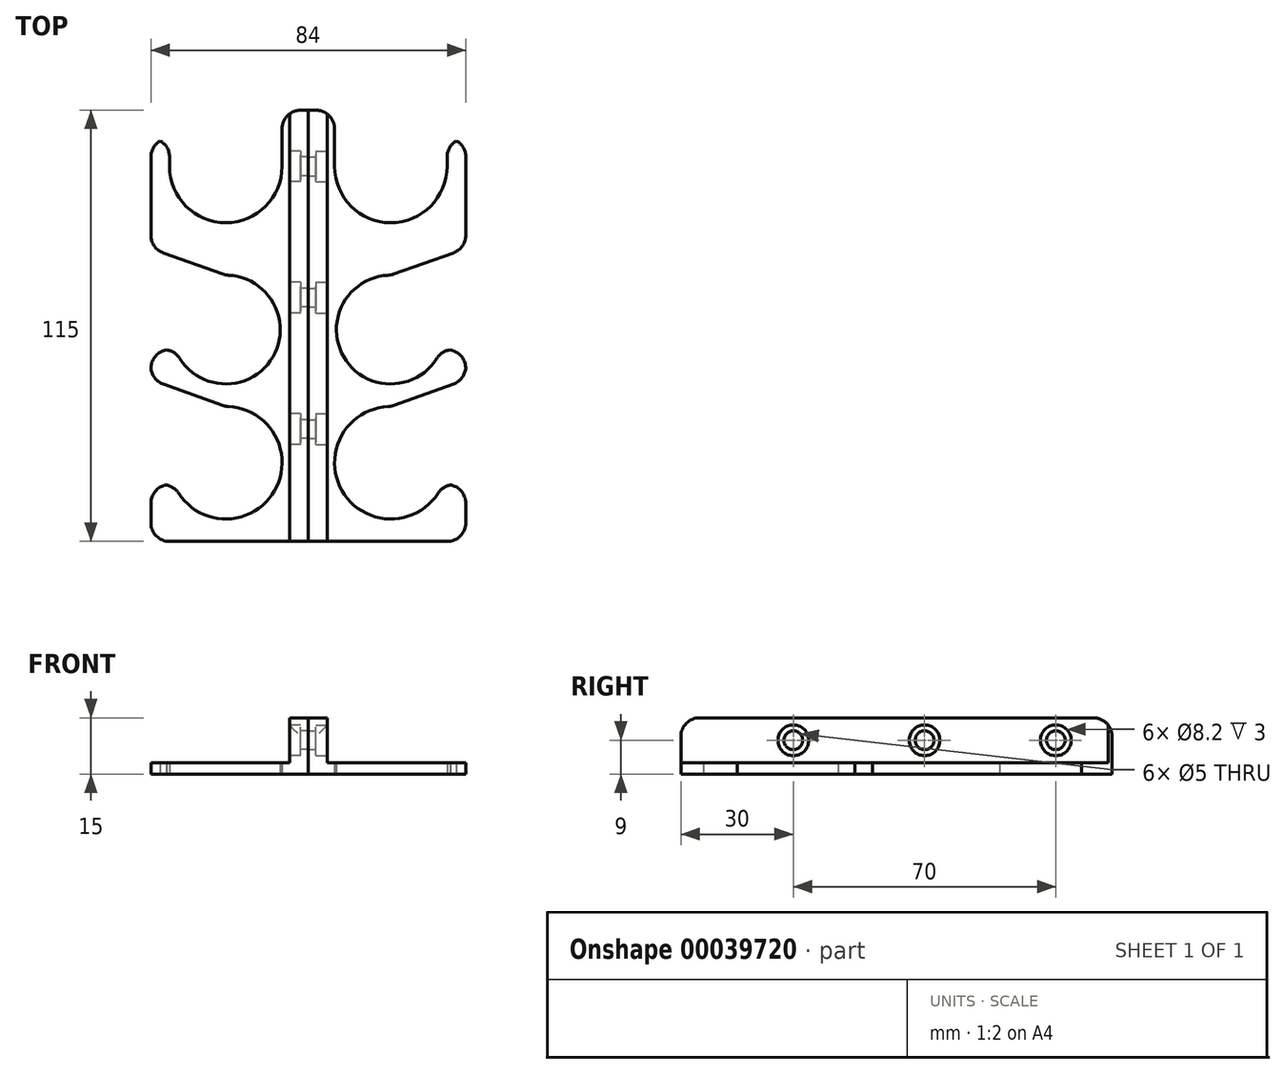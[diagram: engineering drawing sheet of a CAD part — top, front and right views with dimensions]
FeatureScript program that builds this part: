
annotation { "Feature Type Name" : "Feature", "Feature Type Description" : "" }
export const myFeature = defineFeature(function(context is Context, id is Id, definition is map)
    precondition{}
    {
        {
            var Q0;
            Q0=qCreatedBy(makeId("Top.planeOp"),FACE);
            var sketch = newSketch(context, id + "F0", { "sketchPlane" : qUnion([Q0])});
            skLineSegment(sketch, "E0.bottom", {"start": v(0, 0) * mm, "end": v(5, 0) * mm});
            skLineSegment(sketch, "E0.top", {"start": v(0, -115) * mm, "end": v(5, -115) * mm});
            skLineSegment(sketch, "E0.left", {"start": v(0, 0) * mm, "end": v(0, -115) * mm});
            skLineSegment(sketch, "E0.right", {"start": v(5, 0) * mm, "end": v(5, -115) * mm});
            skLineSegment(sketch, "E1.bottom", {"start": v(5, 0) * mm, "end": v(42, 0) * mm});
            skLineSegment(sketch, "E1.top", {"start": v(5, -115) * mm, "end": v(42, -115) * mm});
            skLineSegment(sketch, "E1.right", {"start": v(42, 0) * mm, "end": v(42, -115) * mm});
            skCircle(sketch, "E2", {"center": v(22, -15) * mm, "radius": 15 * mm});
            skCircle(sketch, "E3", {"center": v(22, -58.5) * mm, "radius": 14.5 * mm});
            skCircle(sketch, "E4", {"center": v(22, -94) * mm, "radius": 15 * mm});
            skLineSegment(sketch, "E5", {"start": v(7, -15) * mm, "end": v(7, 0) * mm});
            skLineSegment(sketch, "E6", {"start": v(37, -15) * mm, "end": v(37, 0) * mm});
            skLineSegment(sketch, "E7", {"start": v(35.47, -63.86) * mm, "end": v(42, -63.86) * mm});
            skLineSegment(sketch, "E8", {"start": v(22, -44) * mm, "end": v(42, -36.86) * mm});
            skLineSegment(sketch, "E9", {"start": v(35.82, -99.83) * mm, "end": v(42, -99.83) * mm});
            skLineSegment(sketch, "E10", {"start": v(22, -79) * mm, "end": v(42, -71.83) * mm});
            skLineSegment(sketch, "E11", {"start": v(37, -7.5) * mm, "end": v(42, -7.5) * mm});
            skSolve(sketch);
        }
        {
            var Q0;
            {var subQ4=sQuery(id+"F0.wireOp",EDGE,"E1.top");Q0=makeQuery(id+"F0.imprint","IMPRINT",FACE,{"disambiguationData":[TD([[makeQuery(id+"F0.imprint","IMPRINT",EDGE,{"derivedFrom":subQ4}),1.0]])]});}
            extrude(context, id + "F1", {"entities" : qUnion([Q0]), "depth" : 3 * mm});
        }
        {
            var Q0;
            Q0=makeQuery(id+"F0.imprint","IMPRINT",FACE,{"disambiguationData":[TD([[makeQuery(id+"F0.imprint","IMPRINT",EDGE,{"derivedFrom":sQuery(id+"F0.wireOp",EDGE,"E0.bottom")}),-1.0]])]});
            extrude(context, id + "F2", {"entities" : qUnion([Q0]), "operationType" : NewBodyOperationType.ADD, "depth" : 15 * mm});
        }
        {
            var Q0;
            Q0=makeQuery(id+"F2.opExtrude","SWEPT_FACE",FACE,{"disambiguationData":[OSD([sQuery(id+"F0.wireOp",EDGE,"E0.right")])]});
            var sketch = newSketch(context, id + "F3", { "sketchPlane" : qUnion([Q0])});
            skPoint(sketch, "E12", {"position": v(-100, 9) * mm});
            skLineSegment(sketch, "E13", {"start": v(-100, 9) * mm, "end": v(0, 9) * mm, "construction": true});
            skPoint(sketch, "E14", {"position": v(-50, 9) * mm});
            skPoint(sketch, "E15", {"position": v(-85, 9) * mm});
            skPoint(sketch, "E16", {"position": v(-15, 9) * mm});
            skCircle(sketch, "E17", {"center": v(-85, 9) * mm, "radius": 4.1 * mm});
            skCircle(sketch, "E18", {"center": v(-15, 9) * mm, "radius": 4.1 * mm});
            skCircle(sketch, "E19", {"center": v(-50, 9) * mm, "radius": 4.1 * mm});
            skCircle(sketch, "E20", {"center": v(-85, 9) * mm, "radius": 2.5 * mm});
            skCircle(sketch, "E21", {"center": v(-50, 9) * mm, "radius": 2.5 * mm});
            skCircle(sketch, "E22", {"center": v(-15, 9) * mm, "radius": 2.5 * mm});
            skPoint(sketch, "E23", {"position": v(0, 9) * mm});
            skSolve(sketch);
        }
        {
            var Q0;
            Q0=makeQuery(id+"F3.imprint","IMPRINT",FACE,{"disambiguationData":[TD([[makeQuery(id+"F3.imprint","IMPRINT",EDGE,{"derivedFrom":sQuery(id+"F3.wireOp",EDGE,"E17")}),1.0]])]});
            var Q1;
            Q1=makeQuery(id+"F3.imprint","IMPRINT",FACE,{"disambiguationData":[TD([[makeQuery(id+"F3.imprint","IMPRINT",EDGE,{"derivedFrom":sQuery(id+"F3.wireOp",EDGE,"E19")}),1.0]])]});
            var Q2;
            Q2=makeQuery(id+"F3.imprint","IMPRINT",FACE,{"disambiguationData":[TD([[makeQuery(id+"F3.imprint","IMPRINT",EDGE,{"derivedFrom":sQuery(id+"F3.wireOp",EDGE,"E18")}),1.0]])]});
            extrude(context, id + "F4", {"entities" : qUnion([Q0, Q1, Q2]), "operationType" : NewBodyOperationType.REMOVE, "oppositeDirection" : true, "depth" : 3 * mm});
        }
        {
            var Q0;
            Q0=makeQuery(id+"F4.boolean.opBoolean","SPLIT",FACE,{"disambiguationData":[TD([makeQuery(id+"F4.opExtrude","SWEPT_FACE",FACE,{"disambiguationData":[OSD([sQuery(id+"F3.wireOp",EDGE,"E22")])]})])],"derivedFrom":makeQuery(id+"F2.opExtrude","SWEPT_FACE",FACE,{"disambiguationData":[OSD([sQuery(id+"F0.wireOp",EDGE,"E0.right")])]})});
            var Q1;
            Q1=makeQuery(id+"F4.boolean.opBoolean","SPLIT",FACE,{"disambiguationData":[TD([makeQuery(id+"F4.opExtrude","SWEPT_FACE",FACE,{"disambiguationData":[OSD([sQuery(id+"F3.wireOp",EDGE,"E21")])]})])],"derivedFrom":makeQuery(id+"F2.opExtrude","SWEPT_FACE",FACE,{"disambiguationData":[OSD([sQuery(id+"F0.wireOp",EDGE,"E0.right")])]})});
            var Q2;
            Q2=makeQuery(id+"F4.boolean.opBoolean","SPLIT",FACE,{"disambiguationData":[TD([makeQuery(id+"F4.opExtrude","SWEPT_FACE",FACE,{"disambiguationData":[OSD([sQuery(id+"F3.wireOp",EDGE,"E20")])]})])],"derivedFrom":makeQuery(id+"F2.opExtrude","SWEPT_FACE",FACE,{"disambiguationData":[OSD([sQuery(id+"F0.wireOp",EDGE,"E0.right")])]})});
            extrude(context, id + "F5", {"entities" : qUnion([Q0, Q1, Q2]), "operationType" : NewBodyOperationType.REMOVE, "oppositeDirection" : true, "depth" : 25 * mm});
        }
        {
            var Q0;
            Q0=makeQuery(id+"F1.opExtrude","SWEPT_BODY",BODY,{"disambiguationData":[OSD([sQuery(id+"F0.wireOp",EDGE,"E1.bottom"),sQuery(id+"F0.wireOp",EDGE,"E1.top"),sQuery(id+"F0.wireOp",EDGE,"E0.right"),sQuery(id+"F0.wireOp",EDGE,"E1.right"),sQuery(id+"F0.wireOp",EDGE,"E2"),sQuery(id+"F0.wireOp",EDGE,"E3"),sQuery(id+"F0.wireOp",EDGE,"E4"),sQuery(id+"F0.wireOp",EDGE,"E5"),sQuery(id+"F0.wireOp",EDGE,"E6"),sQuery(id+"F0.wireOp",EDGE,"E7"),sQuery(id+"F0.wireOp",EDGE,"E8"),sQuery(id+"F0.wireOp",EDGE,"E9"),sQuery(id+"F0.wireOp",EDGE,"E10"),sQuery(id+"F0.wireOp",EDGE,"E11")])]});
            var Q1;
            Q1=makeQuery(id+"F2.opExtrude","SWEPT_FACE",FACE,{"disambiguationData":[OSD([sQuery(id+"F0.wireOp",EDGE,"E0.left")])]});
            mirror(context, id + "F6", {"entities" : qUnion([Q0]), "mirrorPlane" : qUnion([Q1])});
        }
        {
            var Q0;
            Q0=makeQuery(id+"F6.opPattern","COPY",EDGE,{"derivedFrom":makeQuery(id+"F1.opExtrude","SWEPT_EDGE",EDGE,{"disambiguationData":[OSD([sQuery(id+"F0.wireOp",EDGE,"E1.top"),sQuery(id+"F0.wireOp",EDGE,"E1.right")])]}),"instanceName":"1"});
            var Q1;
            Q1=makeQuery(id+"F6.opPattern","COPY",EDGE,{"derivedFrom":makeQuery(id+"F1.opExtrude","SWEPT_EDGE",EDGE,{"disambiguationData":[OSD([sQuery(id+"F0.wireOp",EDGE,"E1.right"),sQuery(id+"F0.wireOp",EDGE,"E8")])]}),"instanceName":"1"});
            var Q2;
            Q2=makeQuery(id+"F6.opPattern","COPY",EDGE,{"derivedFrom":makeQuery(id+"F1.opExtrude","SWEPT_EDGE",EDGE,{"disambiguationData":[OSD([sQuery(id+"F0.wireOp",EDGE,"E1.right"),sQuery(id+"F0.wireOp",EDGE,"E10")])]}),"instanceName":"1"});
            var Q3;
            Q3=makeQuery(id+"F6.opPattern","COPY",EDGE,{"derivedFrom":makeQuery(id+"F1.opExtrude","SWEPT_EDGE",EDGE,{"disambiguationData":[OSD([sQuery(id+"F0.wireOp",EDGE,"E1.right"),sQuery(id+"F0.wireOp",EDGE,"E11")])]}),"instanceName":"1"});
            var Q4;
            Q4=makeQuery(id+"F6.opPattern","COPY",EDGE,{"derivedFrom":makeQuery(id+"F1.opExtrude","SWEPT_EDGE",EDGE,{"disambiguationData":[OSD([sQuery(id+"F0.wireOp",EDGE,"E6"),sQuery(id+"F0.wireOp",EDGE,"E11")])]}),"instanceName":"1"});
            var Q5;
            Q5=makeQuery(id+"F6.opPattern","COPY",EDGE,{"derivedFrom":makeQuery(id+"F1.opExtrude","SWEPT_EDGE",EDGE,{"disambiguationData":[OSD([sQuery(id+"F0.wireOp",EDGE,"E1.right"),sQuery(id+"F0.wireOp",EDGE,"E9")])]}),"instanceName":"1"});
            var Q6;
            Q6=makeQuery(id+"F6.opPattern","COPY",EDGE,{"derivedFrom":makeQuery(id+"F1.opExtrude","SWEPT_EDGE",EDGE,{"disambiguationData":[OSD([sQuery(id+"F0.wireOp",EDGE,"E3"),sQuery(id+"F0.wireOp",EDGE,"E7")])]}),"instanceName":"1"});
            var Q7;
            Q7=makeQuery(id+"F6.opPattern","COPY",EDGE,{"derivedFrom":makeQuery(id+"F1.opExtrude","SWEPT_EDGE",EDGE,{"disambiguationData":[OSD([sQuery(id+"F0.wireOp",EDGE,"E4"),sQuery(id+"F0.wireOp",EDGE,"E9")])]}),"instanceName":"1"});
            var Q8;
            Q8=makeQuery(id+"F6.opPattern","COPY",EDGE,{"derivedFrom":makeQuery(id+"F1.opExtrude","SWEPT_EDGE",EDGE,{"disambiguationData":[OSD([sQuery(id+"F0.wireOp",EDGE,"E1.right"),sQuery(id+"F0.wireOp",EDGE,"E7")])]}),"instanceName":"1"});
            var Q9;
            Q9=makeQuery(id+"F6.opPattern","COPY",EDGE,{"derivedFrom":makeQuery(id+"F1.opExtrude","SWEPT_EDGE",EDGE,{"disambiguationData":[OSD([sQuery(id+"F0.wireOp",EDGE,"E4"),sQuery(id+"F0.wireOp",EDGE,"E10")])]}),"instanceName":"1"});
            var Q10;
            Q10=makeQuery(id+"F6.opPattern","COPY",EDGE,{"derivedFrom":makeQuery(id+"F1.opExtrude","SWEPT_EDGE",EDGE,{"disambiguationData":[OSD([sQuery(id+"F0.wireOp",EDGE,"E3"),sQuery(id+"F0.wireOp",EDGE,"E8")])]}),"instanceName":"1"});
            var Q11;
            Q11=makeQuery(id+"F6.opPattern","COPY",EDGE,{"derivedFrom":makeQuery(id+"F1.opExtrude","SWEPT_EDGE",EDGE,{"disambiguationData":[OSD([sQuery(id+"F0.wireOp",EDGE,"E1.bottom"),sQuery(id+"F0.wireOp",EDGE,"E5")])]}),"instanceName":"1"});
            var Q12;
            Q12=makeQuery(id+"F6.opPattern","COPY",EDGE,{"derivedFrom":makeQuery(id+"F2.opExtrude","CAP_EDGE",EDGE,{"disambiguationData":[OSD([sQuery(id+"F0.wireOp",EDGE,"E0.bottom")])],"isStart":false}),"instanceName":"1"});
            var Q13;
            Q13=makeQuery(id+"F6.opPattern","COPY",EDGE,{"derivedFrom":makeQuery(id+"F2.opExtrude","CAP_EDGE",EDGE,{"disambiguationData":[OSD([sQuery(id+"F0.wireOp",EDGE,"E0.top")])],"isStart":false}),"instanceName":"1"});
            fillet(context, id + "F7", {"entities" : qUnion([Q0, Q1, Q2, Q3, Q4, Q5, Q6, Q7, Q8, Q9, Q10, Q11, Q12, Q13]), "radius" : 5 * mm, "tangentPropagation" : true, "allowEdgeOverflow" : false});
        }
        {
            var Q0;
            Q0=makeQuery(id+"F2.opExtrude","CAP_EDGE",EDGE,{"disambiguationData":[OSD([sQuery(id+"F0.wireOp",EDGE,"E0.top")])],"isStart":false});
            var Q1;
            Q1=makeQuery(id+"F1.opExtrude","SWEPT_EDGE",EDGE,{"disambiguationData":[OSD([sQuery(id+"F0.wireOp",EDGE,"E1.top"),sQuery(id+"F0.wireOp",EDGE,"E1.right")])]});
            var Q2;
            Q2=makeQuery(id+"F1.opExtrude","SWEPT_EDGE",EDGE,{"disambiguationData":[OSD([sQuery(id+"F0.wireOp",EDGE,"E1.right"),sQuery(id+"F0.wireOp",EDGE,"E9")])]});
            var Q3;
            Q3=makeQuery(id+"F1.opExtrude","SWEPT_EDGE",EDGE,{"disambiguationData":[OSD([sQuery(id+"F0.wireOp",EDGE,"E1.right"),sQuery(id+"F0.wireOp",EDGE,"E10")])]});
            var Q4;
            Q4=makeQuery(id+"F1.opExtrude","SWEPT_EDGE",EDGE,{"disambiguationData":[OSD([sQuery(id+"F0.wireOp",EDGE,"E1.right"),sQuery(id+"F0.wireOp",EDGE,"E7")])]});
            var Q5;
            Q5=makeQuery(id+"F1.opExtrude","SWEPT_EDGE",EDGE,{"disambiguationData":[OSD([sQuery(id+"F0.wireOp",EDGE,"E1.right"),sQuery(id+"F0.wireOp",EDGE,"E8")])]});
            var Q6;
            Q6=makeQuery(id+"F1.opExtrude","SWEPT_EDGE",EDGE,{"disambiguationData":[OSD([sQuery(id+"F0.wireOp",EDGE,"E3"),sQuery(id+"F0.wireOp",EDGE,"E8")])]});
            var Q7;
            Q7=makeQuery(id+"F1.opExtrude","SWEPT_EDGE",EDGE,{"disambiguationData":[OSD([sQuery(id+"F0.wireOp",EDGE,"E4"),sQuery(id+"F0.wireOp",EDGE,"E10")])]});
            var Q8;
            Q8=makeQuery(id+"F1.opExtrude","SWEPT_EDGE",EDGE,{"disambiguationData":[OSD([sQuery(id+"F0.wireOp",EDGE,"E4"),sQuery(id+"F0.wireOp",EDGE,"E9")])]});
            var Q9;
            Q9=makeQuery(id+"F1.opExtrude","SWEPT_EDGE",EDGE,{"disambiguationData":[OSD([sQuery(id+"F0.wireOp",EDGE,"E6"),sQuery(id+"F0.wireOp",EDGE,"E11")])]});
            var Q10;
            Q10=makeQuery(id+"F1.opExtrude","SWEPT_EDGE",EDGE,{"disambiguationData":[OSD([sQuery(id+"F0.wireOp",EDGE,"E1.right"),sQuery(id+"F0.wireOp",EDGE,"E11")])]});
            var Q11;
            Q11=makeQuery(id+"F1.opExtrude","SWEPT_EDGE",EDGE,{"disambiguationData":[OSD([sQuery(id+"F0.wireOp",EDGE,"E1.bottom"),sQuery(id+"F0.wireOp",EDGE,"E5")])]});
            var Q12;
            Q12=makeQuery(id+"F1.opExtrude","SWEPT_EDGE",EDGE,{"disambiguationData":[OSD([sQuery(id+"F0.wireOp",EDGE,"E3"),sQuery(id+"F0.wireOp",EDGE,"E7")])]});
            var Q13;
            Q13=makeQuery(id+"F2.opExtrude","CAP_EDGE",EDGE,{"disambiguationData":[OSD([sQuery(id+"F0.wireOp",EDGE,"E0.bottom")])],"isStart":false});
            fillet(context, id + "F8", {"entities" : qUnion([Q0, Q1, Q2, Q3, Q4, Q5, Q6, Q7, Q8, Q9, Q10, Q11, Q12, Q13]), "radius" : 5 * mm, "tangentPropagation" : true, "allowEdgeOverflow" : false});
        }
    });
